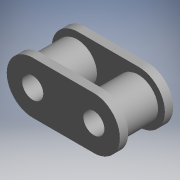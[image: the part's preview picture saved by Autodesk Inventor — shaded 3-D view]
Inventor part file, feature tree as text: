
AUTODESK INVENTOR PART (.ipt)
format: ipt  version: 2019 (Build 230136000, 136)  size: 160,256 bytes
history: native  units: mm (DEFAULTED — no unit token found)
features: other x14, sketch x4, revolve x2, extrude x2
ambient origin geometry x8: Origin, YZ Plane, XZ Plane, XY Plane, X Axis, Y Axis, Z Axis, Center Point
bodies: Solid1 (feature_tree)
feature tree (22):
  revolve  "Revolution1"  [1 undecoded]
  extrude  "Extrusion1"  TaperAngle=360.0deg  [1 undecoded]
  extrude  "Extrusion2"  [1 undecoded]
  revolve  "Revolution2"  [1 undecoded]
  other  "for_body1_a_XY"
  other  "for_body1_a_YZ"
  other  "for_body1_a_ZX"
  other  "for_body1_a_X"
  other  "for_body1_a_Y"
  other  "for_body1_a_Z"
  other  "for_body1_a_Center"
  other  "to_dummy_XY"
  other  "to_dummy_YZ"
  other  "to_dummy_ZX"
  other  "to_dummy_X"
  other  "to_dummy_Y"
  other  "to_dummy_Z"
  other  "to_dummy_Center"
  sketch  "Sketch_2"  dims[d0=360.0deg d1=1.3mm d2=0.0mm]
  sketch  "Sketch_5"  dims[d3=1.3mm d4=0.0mm d5=360.0deg]
  sketch  "Sketch_6"
  sketch  "Sketch_8"
note: 4 required parameter values undecoded (feature->parameter linkage not recoverable at this tier; creation-order binding heuristic only, values carry confidence <= 0.55)